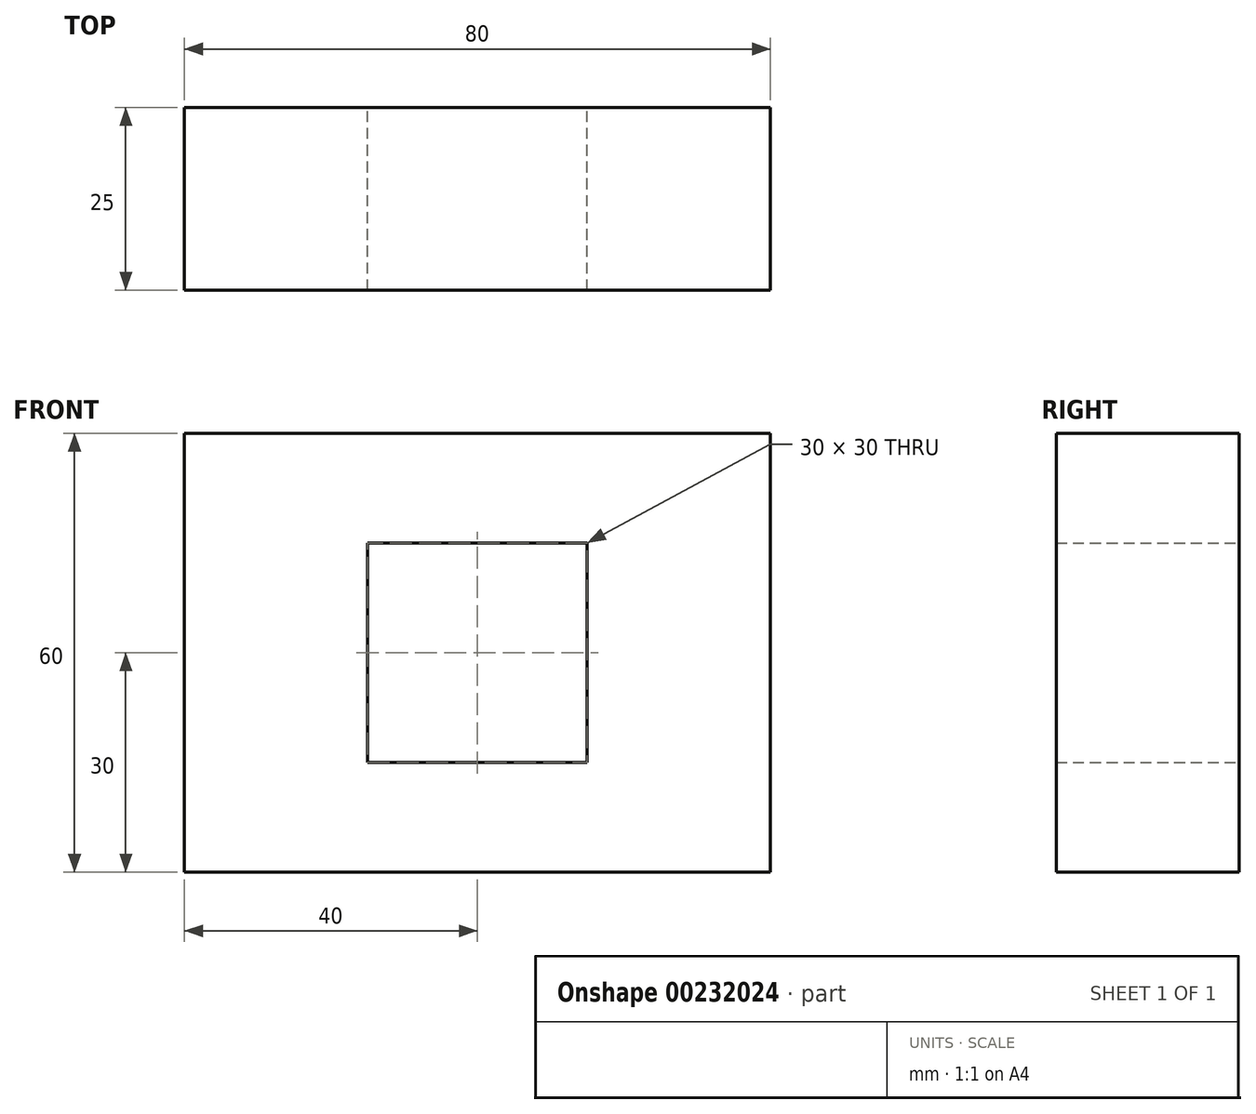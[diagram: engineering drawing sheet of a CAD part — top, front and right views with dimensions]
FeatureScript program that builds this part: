
annotation { "Feature Type Name" : "Feature", "Feature Type Description" : "" }
export const myFeature = defineFeature(function(context is Context, id is Id, definition is map)
    precondition{}
    {
        {
            var Q0;
            Q0=qCreatedBy(makeId("Front.planeOp"),FACE);
            var sketch = newSketch(context, id + "F0", { "sketchPlane" : qUnion([Q0])});
            skLineSegment(sketch, "E0.bottom", {"start": v(-40, 30) * mm, "end": v(40, 30) * mm});
            skLineSegment(sketch, "E0.top", {"start": v(-40, -30) * mm, "end": v(40, -30) * mm});
            skLineSegment(sketch, "E0.left", {"start": v(-40, 30) * mm, "end": v(-40, -30) * mm});
            skLineSegment(sketch, "E0.right", {"start": v(40, 30) * mm, "end": v(40, -30) * mm});
            skPoint(sketch, "E0.middle", {"position": v(0, 0) * mm});
            skLineSegment(sketch, "E1.bottom", {"start": v(-15, 15) * mm, "end": v(15, 15) * mm});
            skLineSegment(sketch, "E1.top", {"start": v(-15, -15) * mm, "end": v(15, -15) * mm});
            skLineSegment(sketch, "E1.left", {"start": v(-15, 15) * mm, "end": v(-15, -15) * mm});
            skLineSegment(sketch, "E1.right", {"start": v(15, 15) * mm, "end": v(15, -15) * mm});
            skSolve(sketch);
        }
        {
            var Q0;
            Q0=makeQuery(id+"F0.imprint","IMPRINT",FACE,{"disambiguationData":[TD([[makeQuery(id+"F0.imprint","IMPRINT",EDGE,{"derivedFrom":sQuery(id+"F0.wireOp",EDGE,"E0.bottom")}),-1.0]])]});
            extrude(context, id + "F1", {"entities" : qUnion([Q0]), "depth" : 25 * mm});
        }
    });
